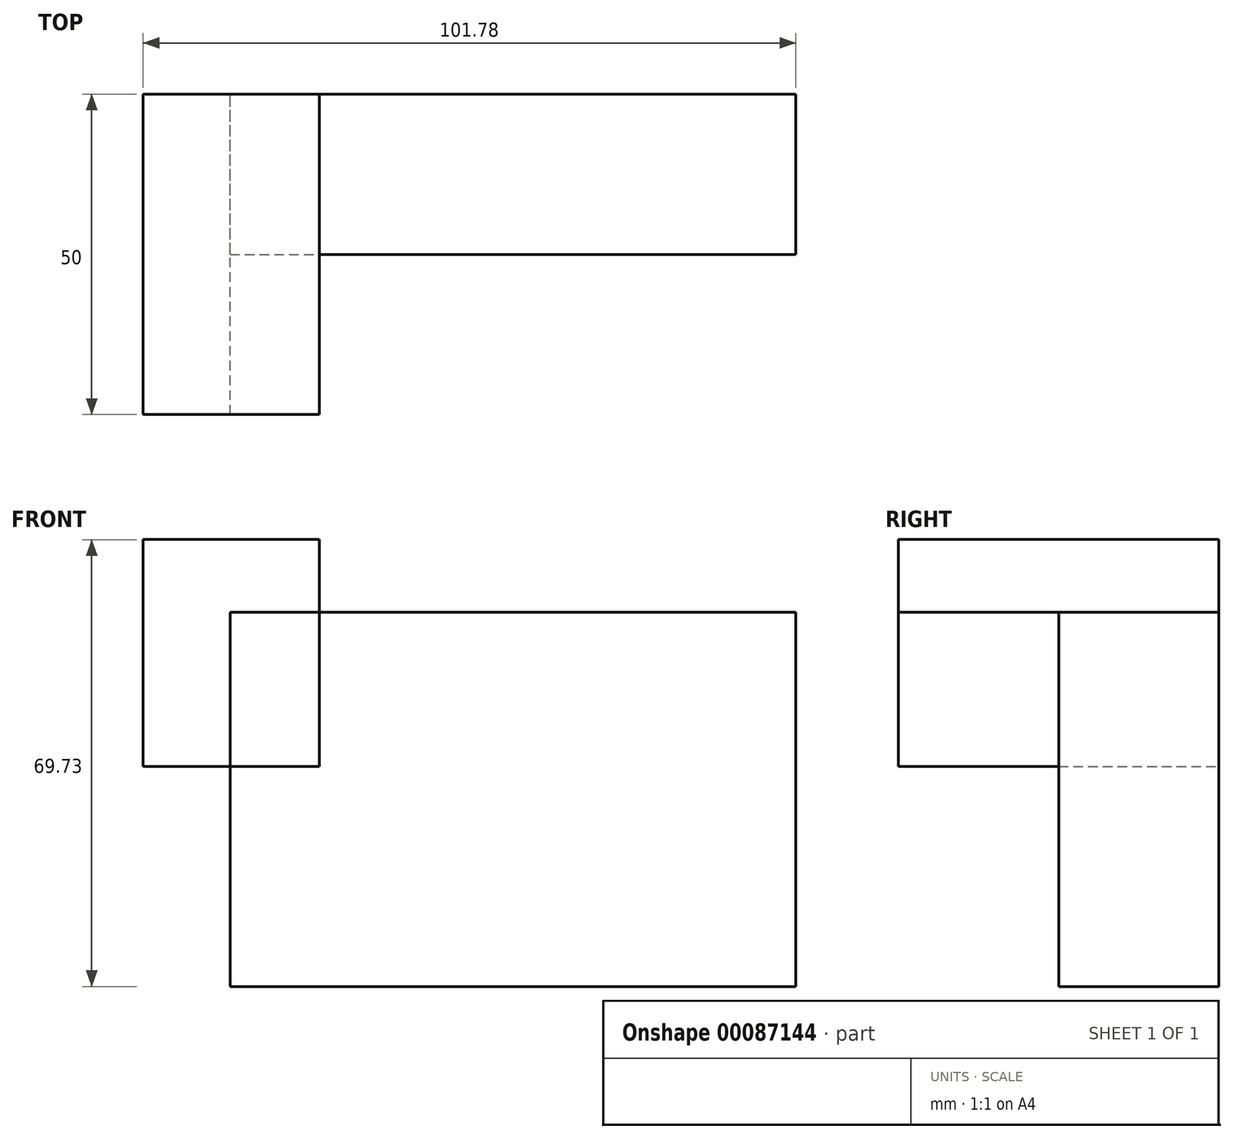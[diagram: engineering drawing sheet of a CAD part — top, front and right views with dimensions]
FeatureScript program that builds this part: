
annotation { "Feature Type Name" : "Feature", "Feature Type Description" : "" }
export const myFeature = defineFeature(function(context is Context, id is Id, definition is map)
    precondition{}
    {
        {
            var Q0;
            Q0=qCreatedBy(makeId("Front.planeOp"),FACE);
            var sketch = newSketch(context, id + "F0", { "sketchPlane" : qUnion([Q0])});
            skLineSegment(sketch, "E0.bottom", {"start": v(-37.5, 27.24) * mm, "end": v(50.7, 27.24) * mm});
            skLineSegment(sketch, "E0.top", {"start": v(-37.5, -31.2) * mm, "end": v(50.7, -31.2) * mm});
            skLineSegment(sketch, "E0.left", {"start": v(-37.5, 27.24) * mm, "end": v(-37.5, -31.2) * mm});
            skLineSegment(sketch, "E0.right", {"start": v(50.7, 27.24) * mm, "end": v(50.7, -31.2) * mm});
            skLineSegment(sketch, "E1.bottom", {"start": v(-12.63, 27.24) * mm, "end": v(-12.82, 27.24) * mm});
            skLineSegment(sketch, "E1.top", {"start": v(-12.63, 31.38) * mm, "end": v(-12.82, 31.38) * mm});
            skLineSegment(sketch, "E1.left", {"start": v(-12.63, 27.24) * mm, "end": v(-12.63, 31.38) * mm});
            skLineSegment(sketch, "E1.right", {"start": v(-12.82, 27.24) * mm, "end": v(-12.82, 31.38) * mm});
            skLineSegment(sketch, "E2.bottom", {"start": v(-51.08, 38.54) * mm, "end": v(-23.56, 38.54) * mm});
            skLineSegment(sketch, "E2.top", {"start": v(-51.08, 3.1) * mm, "end": v(-23.56, 3.1) * mm});
            skLineSegment(sketch, "E2.left", {"start": v(-51.08, 38.54) * mm, "end": v(-51.08, 3.1) * mm});
            skLineSegment(sketch, "E2.right", {"start": v(-23.56, 38.54) * mm, "end": v(-23.56, 3.1) * mm});
            skSolve(sketch);
        }
        {
            var Q0;
            {var subQ4=sQuery(id+"F0.wireOp",EDGE,"E2.bottom");Q0=makeQuery(id+"F0.imprint","IMPRINT",FACE,{"disambiguationData":[TD([[makeQuery(id+"F0.imprint","IMPRINT",EDGE,{"derivedFrom":subQ4}),-1.0]])]});}
            var Q1;
            {var subQ1=sQuery(id+"F0.wireOp",EDGE,"E0.top");Q1=makeQuery(id+"F0.imprint","IMPRINT",FACE,{"disambiguationData":[TD([[makeQuery(id+"F0.imprint","IMPRINT",EDGE,{"derivedFrom":subQ1}),1.0]])]});}
            extrude(context, id + "F1", {"entities" : qUnion([Q0, Q1]), "depth" : 25 * mm});
        }
        {
            var Q0;
            Q0=makeQuery(id+"F1.opExtrude","CAP_FACE",FACE,{"disambiguationData":[OSD([sQuery(id+"F0.wireOp",EDGE,"E0.bottom"),sQuery(id+"F0.wireOp",EDGE,"E0.left"),sQuery(id+"F0.wireOp",EDGE,"E2.bottom"),sQuery(id+"F0.wireOp",EDGE,"E2.top"),sQuery(id+"F0.wireOp",EDGE,"E2.left"),sQuery(id+"F0.wireOp",EDGE,"E2.right")])],"isStart":false});
            extrude(context, id + "F2", {"entities" : qUnion([Q0]), "operationType" : NewBodyOperationType.ADD, "depth" : 25 * mm});
        }
    });
